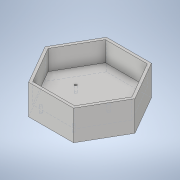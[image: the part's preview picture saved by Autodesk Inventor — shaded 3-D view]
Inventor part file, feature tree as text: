
AUTODESK INVENTOR PART (.ipt)
format: ipt  version: 2020.2 (Build 242310000, 310)  size: 162,304 bytes
history: native  units: in
note: dims shown in document units (in); Inventor stores cm internally (conversion verified against a paired STEP export)
features: extrude x4, sketch x4
ambient origin geometry x8: Origin, YZ Plane, XZ Plane, XY Plane, X Axis, Y Axis, Z Axis, Center Point
bodies: Solid1 (feature_tree)
feature tree (8):
  extrude  "Extrusion1"  Depth=2.25in
  extrude  "Extrusion2"  Depth=2.25in
  extrude  "Extrusion3"  Depth=1.5in
  extrude  "Extrusion4"  TaperAngle=60.0deg  [1 undecoded]
  sketch  "Sketch1"  dims[d0=2.25in d1=2.25in]
  sketch  "Sketch2"  dims[d2=2.25in d3=2.25in]
  sketch  "Sketch3"  dims[d4=1.5in d5=0.0in d6=2.1in]
  sketch  "Sketch4"  dims[d7=2.1in d8=60.0deg d9=2.1in d10=2.1in d11=1.25in d12=0.0in d13=0.25in d14=0.0in d15=0.1181in d16=0.1752in d17=0.1181in d18=1.65in d19=0.825in d20=0.1752in d21=0.1181in d22=1.7514in d23=0.825in d24=0.1181in d25=1.65in d26=1.7514in d27=0.3333in d28=0.0in]
note: 1 required parameter value undecoded (feature->parameter linkage not recoverable at this tier; creation-order binding heuristic only, values carry confidence <= 0.55)
